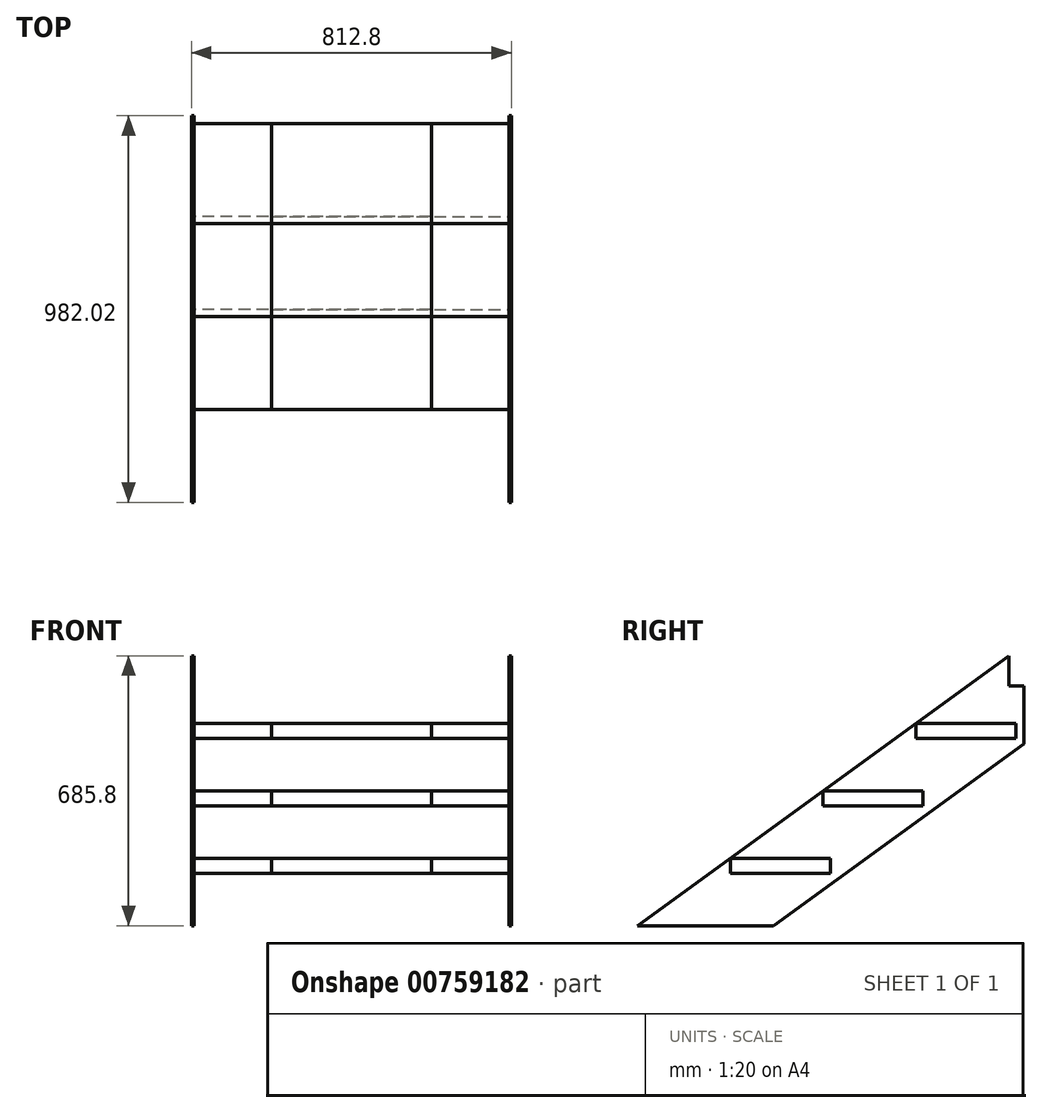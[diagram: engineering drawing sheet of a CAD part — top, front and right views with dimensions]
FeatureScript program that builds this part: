
annotation { "Feature Type Name" : "Feature", "Feature Type Description" : "" }
export const myFeature = defineFeature(function(context is Context, id is Id, definition is map)
    precondition{}
    {
        {
            var Q0;
            Q0=qCreatedBy(makeId("Right.planeOp"),FACE);
            var sketch = newSketch(context, id + "F0", { "sketchPlane" : qUnion([Q0])});
            skLineSegment(sketch, "E0", {"start": v(0, 0) * mm, "end": v(-943.92, 0) * mm});
            skLineSegment(sketch, "E1", {"start": v(0, 685.8) * mm, "end": v(-943.92, 0) * mm});
            skLineSegment(sketch, "E2", {"start": v(-598.22, 0) * mm, "end": v(0, 434.63) * mm});
            skLineSegment(sketch, "E3.bottom", {"start": v(-707.94, 171.45) * mm, "end": v(-453.94, 171.45) * mm});
            skLineSegment(sketch, "E3.top", {"start": v(-707.94, 133.35) * mm, "end": v(-453.94, 133.35) * mm});
            skLineSegment(sketch, "E3.left", {"start": v(-707.94, 171.45) * mm, "end": v(-707.94, 133.35) * mm});
            skLineSegment(sketch, "E3.right", {"start": v(-453.94, 171.45) * mm, "end": v(-453.94, 133.35) * mm});
            skLineSegment(sketch, "E4.bottom", {"start": v(-471.96, 342.9) * mm, "end": v(-217.96, 342.9) * mm});
            skLineSegment(sketch, "E4.top", {"start": v(-471.96, 304.8) * mm, "end": v(-217.96, 304.8) * mm});
            skLineSegment(sketch, "E4.left", {"start": v(-471.96, 342.9) * mm, "end": v(-471.96, 304.8) * mm});
            skLineSegment(sketch, "E4.right", {"start": v(-217.96, 342.9) * mm, "end": v(-217.96, 304.8) * mm});
            skLineSegment(sketch, "E5", {"start": v(0, 685.8) * mm, "end": v(0, 0) * mm});
            skLineSegment(sketch, "E6.bottom", {"start": v(-235.98, 514.35) * mm, "end": v(18.02, 514.35) * mm});
            skLineSegment(sketch, "E6.top", {"start": v(-235.98, 476.25) * mm, "end": v(18.02, 476.25) * mm});
            skLineSegment(sketch, "E6.left", {"start": v(-235.98, 514.35) * mm, "end": v(-235.98, 476.25) * mm});
            skLineSegment(sketch, "E6.right", {"start": v(18.02, 514.35) * mm, "end": v(18.02, 476.25) * mm});
            skLineSegment(sketch, "E7", {"start": v(0, 609.6) * mm, "end": v(38.1, 609.6) * mm});
            skLineSegment(sketch, "E8", {"start": v(38.1, 609.6) * mm, "end": v(38.1, 462.31) * mm});
            skLineSegment(sketch, "E9", {"start": v(38.1, 462.31) * mm, "end": v(0, 434.63) * mm});
            skSolve(sketch);
        }
        {
            var Q0;
            {var subQ15=sQuery(id+"F0.wireOp",EDGE,"E3.top");Q0=makeQuery(id+"F0.imprint","IMPRINT",FACE,{"disambiguationData":[TD([[makeQuery(id+"F0.imprint","IMPRINT",EDGE,{"derivedFrom":subQ15}),-1.0]])]});}
            var Q1;
            {var subQ0=sQuery(id+"F0.wireOp",EDGE,"8nGeiQJS-kXjl-ygCf-tkNA-O2oD8sTWfOC5");var subQ1=sQuery(id+"F0.wireOp",EDGE,"E4.bottom");var subQ2=makeQuery(id+"F0.imprint","INTERSECT",VERTEX,{"derivedFrom":[subQ1,subQ0]});Q1=makeQuery(id+"F0.imprint","IMPRINT",FACE,{"disambiguationData":[TD([[makeQuery(id+"F0.imprint","IMPRINT",EDGE,{"disambiguationData":[TD([[subQ2,1.0]])],"derivedFrom":subQ1}),1.0]])]});}
            var Q2;
            {var subQ1=sQuery(id+"F0.wireOp",EDGE,"E4.top");Q2=makeQuery(id+"F0.imprint","IMPRINT",FACE,{"disambiguationData":[TD([[makeQuery(id+"F0.imprint","IMPRINT",EDGE,{"derivedFrom":subQ1}),1.0]])]});}
            var Q3;
            {var subQ2=sQuery(id+"F0.wireOp",EDGE,"E3.top");Q3=makeQuery(id+"F0.imprint","IMPRINT",FACE,{"disambiguationData":[TD([[makeQuery(id+"F0.imprint","IMPRINT",EDGE,{"derivedFrom":subQ2}),1.0]])]});}
            var Q4;
            {var subQ0=sQuery(id+"F0.wireOp",EDGE,"E3.bottom");var subQ5=sQuery(id+"F0.wireOp",EDGE,"nGp2zIO6-5YUV-txhC-nwUu-UrbXQL7LYUXX");var subQ6=makeQuery(id+"F0.imprint","INTERSECT",VERTEX,{"derivedFrom":[subQ0,subQ5]});Q4=makeQuery(id+"F0.imprint","IMPRINT",FACE,{"disambiguationData":[TD([[makeQuery(id+"F0.imprint","IMPRINT",EDGE,{"disambiguationData":[TD([[subQ6,-1.0]])],"derivedFrom":subQ5}),1.0]])]});}
            var Q5;
            {var subQ1=sQuery(id+"F0.wireOp",EDGE,"E4.bottom");var subQ3=sQuery(id+"F0.wireOp",EDGE,"nGp2zIO6-5YUV-txhC-nwUu-UrbXQL7LYUXX");var subQ4=makeQuery(id+"F0.imprint","INTERSECT",VERTEX,{"derivedFrom":[subQ1,subQ3]});Q5=makeQuery(id+"F0.imprint","IMPRINT",FACE,{"disambiguationData":[TD([[makeQuery(id+"F0.imprint","IMPRINT",EDGE,{"disambiguationData":[TD([[subQ4,1.0]])],"derivedFrom":subQ3}),1.0]])]});}
            var Q6;
            {var subQ5=sQuery(id+"F0.wireOp",EDGE,"nGp2zIO6-5YUV-txhC-nwUu-UrbXQL7LYUXX");var subQ6=sQuery(id+"F0.wireOp",EDGE,"E4.bottom");var subQ7=makeQuery(id+"F0.imprint","INTERSECT",VERTEX,{"derivedFrom":[subQ6,subQ5]});Q6=makeQuery(id+"F0.imprint","IMPRINT",FACE,{"disambiguationData":[TD([[makeQuery(id+"F0.imprint","IMPRINT",EDGE,{"disambiguationData":[TD([[subQ7,-1.0]])],"derivedFrom":subQ6}),-1.0]])]});}
            var Q7;
            {var subQ0=sQuery(id+"F0.wireOp",EDGE,"nGp2zIO6-5YUV-txhC-nwUu-UrbXQL7LYUXX");var subQ1=sQuery(id+"F0.wireOp",EDGE,"E4.bottom");var subQ2=makeQuery(id+"F0.imprint","INTERSECT",VERTEX,{"derivedFrom":[subQ1,subQ0]});Q7=makeQuery(id+"F0.imprint","IMPRINT",FACE,{"disambiguationData":[TD([[makeQuery(id+"F0.imprint","IMPRINT",EDGE,{"disambiguationData":[TD([[subQ2,-1.0]])],"derivedFrom":subQ1}),1.0]])]});}
            var Q8;
            {var subQ5=sQuery(id+"F0.wireOp",EDGE,"E2");Q8=makeQuery(id+"F0.imprint","IMPRINT",FACE,{"disambiguationData":[TD([[makeQuery(id+"F0.imprint","IMPRINT",EDGE,{"derivedFrom":subQ5}),1.0]])]});}
            var Q9;
            {var subQ1=sQuery(id+"F0.wireOp",EDGE,"E3.bottom");var subQ3=sQuery(id+"F0.wireOp",EDGE,"nGp2zIO6-5YUV-txhC-nwUu-UrbXQL7LYUXX");var subQ4=makeQuery(id+"F0.imprint","INTERSECT",VERTEX,{"derivedFrom":[subQ1,subQ3]});Q9=makeQuery(id+"F0.imprint","IMPRINT",FACE,{"disambiguationData":[TD([[makeQuery(id+"F0.imprint","IMPRINT",EDGE,{"disambiguationData":[TD([[subQ4,1.0]])],"derivedFrom":subQ3}),1.0]])]});}
            var Q10;
            {var subQ1=sQuery(id+"F0.wireOp",EDGE,"E0");var subQ5=sQuery(id+"F0.wireOp",EDGE,"E1");var subQ8=makeQuery(id+"F0.imprint","INTERSECT",VERTEX,{"derivedFrom":[subQ1,subQ5]});Q10=makeQuery(id+"F0.imprint","IMPRINT",FACE,{"disambiguationData":[TD([[makeQuery(id+"F0.imprint","IMPRINT",EDGE,{"disambiguationData":[TD([[subQ8,1.0]])],"derivedFrom":subQ1}),-1.0]])]});}
            var Q11;
            {var subQ5=sQuery(id+"F0.wireOp",EDGE,"E6.left");Q11=makeQuery(id+"F0.imprint","IMPRINT",FACE,{"disambiguationData":[TD([[makeQuery(id+"F0.imprint","IMPRINT",EDGE,{"derivedFrom":subQ5}),1.0]])]});}
            var Q12;
            {var subQ0=sQuery(id+"F0.wireOp",EDGE,"E5");var subQ1=sQuery(id+"F0.wireOp",EDGE,"E1");var subQ2=makeQuery(id+"F0.imprint","INTERSECT",VERTEX,{"derivedFrom":[subQ1,subQ0]});Q12=makeQuery(id+"F0.imprint","IMPRINT",FACE,{"disambiguationData":[TD([[makeQuery(id+"F0.imprint","IMPRINT",EDGE,{"disambiguationData":[TD([[subQ2,-1.0]])],"derivedFrom":subQ0}),-1.0]])]});}
            var Q13;
            {var subQ0=sQuery(id+"F0.wireOp",EDGE,"E6.right");Q13=makeQuery(id+"F0.imprint","IMPRINT",FACE,{"disambiguationData":[TD([[makeQuery(id+"F0.imprint","IMPRINT",EDGE,{"derivedFrom":subQ0}),1.0]])]});}
            var Q14;
            {var subQ5=sQuery(id+"F0.wireOp",EDGE,"E6.right");Q14=makeQuery(id+"F0.imprint","IMPRINT",FACE,{"disambiguationData":[TD([[makeQuery(id+"F0.imprint","IMPRINT",EDGE,{"derivedFrom":subQ5}),-1.0]])]});}
            extrude(context, id + "F1", {"entities" : qUnion([Q0, Q1, Q2, Q3, Q4, Q5, Q6, Q7, Q8, Q9, Q10, Q11, Q12, Q13, Q14]), "oppositeDirection" : true, "depth" : 6.35 * mm, "offsetDistance" : 25.4 * mm});
        }
        {
            var Q0;
            Q0=qCreatedBy(makeId("Right.planeOp"),FACE);
            cPlane(context, id + "F2", {"entities" : qUnion([Q0]), "cplaneType" : CPlaneType.OFFSET, "offset" : 406.4 * mm, "oppositeDirection" : true, "width" : 152.4 * mm, "height" : 152.4 * mm});
        }
        {
            var Q0;
            {var subQ1=sQuery(id+"F0.wireOp",EDGE,"E4.top");Q0=makeQuery(id+"F0.imprint","IMPRINT",FACE,{"disambiguationData":[TD([[makeQuery(id+"F0.imprint","IMPRINT",EDGE,{"derivedFrom":subQ1}),1.0]])]});}
            var Q1;
            {var subQ2=sQuery(id+"F0.wireOp",EDGE,"E3.top");Q1=makeQuery(id+"F0.imprint","IMPRINT",FACE,{"disambiguationData":[TD([[makeQuery(id+"F0.imprint","IMPRINT",EDGE,{"derivedFrom":subQ2}),1.0]])]});}
            var Q2;
            {var subQ5=sQuery(id+"F0.wireOp",EDGE,"nGp2zIO6-5YUV-txhC-nwUu-UrbXQL7LYUXX");var subQ6=sQuery(id+"F0.wireOp",EDGE,"E4.bottom");var subQ7=makeQuery(id+"F0.imprint","INTERSECT",VERTEX,{"derivedFrom":[subQ6,subQ5]});Q2=makeQuery(id+"F0.imprint","IMPRINT",FACE,{"disambiguationData":[TD([[makeQuery(id+"F0.imprint","IMPRINT",EDGE,{"disambiguationData":[TD([[subQ7,-1.0]])],"derivedFrom":subQ6}),-1.0]])]});}
            var Q3;
            {var subQ5=sQuery(id+"F0.wireOp",EDGE,"E6.left");Q3=makeQuery(id+"F0.imprint","IMPRINT",FACE,{"disambiguationData":[TD([[makeQuery(id+"F0.imprint","IMPRINT",EDGE,{"derivedFrom":subQ5}),1.0]])]});}
            var Q4;
            {var subQ5=sQuery(id+"F0.wireOp",EDGE,"E6.right");Q4=makeQuery(id+"F0.imprint","IMPRINT",FACE,{"disambiguationData":[TD([[makeQuery(id+"F0.imprint","IMPRINT",EDGE,{"derivedFrom":subQ5}),-1.0]])]});}
            extrude(context, id + "F3", {"entities" : qUnion([Q0, Q1, Q2, Q3, Q4]), "oppositeDirection" : true, "depth" : 609.6 * mm, "offsetDistance" : 25.4 * mm});
        }
        {
            var Q0;
            Q0=qCreatedBy(makeId("Front.planeOp"),FACE);
            var sketch = newSketch(context, id + "F4", { "sketchPlane" : qUnion([Q0])});
            skCircle(sketch, "E10", {"center": v(-19.05, 644.53) * mm, "radius": 11.11 * mm});
            skSolve(sketch);
        }
        {
            var Q0;
            Q0 = qSketchRegion(id + "F4", true);
            extrude(context, id + "F5", {"entities" : qUnion([Q0]), "operationType" : NewBodyOperationType.REMOVE, "depth" : 12.7 * mm, "offsetDistance" : 25.4 * mm});
        }
        {
            var Q0;
            Q0=makeQuery(id+"F1.opExtrude","SWEPT_BODY",BODY,{"disambiguationData":[OSD([sQuery(id+"F0.wireOp",EDGE,"E0"),sQuery(id+"F0.wireOp",EDGE,"E1"),sQuery(id+"F0.wireOp",EDGE,"E2"),sQuery(id+"F0.wireOp",EDGE,"E5")])]});
            var Q1;
            Q1=makeQuery(id+"F3.opExtrude","SWEPT_BODY",BODY,{"disambiguationData":[OSD([sQuery(id+"F0.wireOp",EDGE,"E4.bottom"),sQuery(id+"F0.wireOp",EDGE,"E4.top"),sQuery(id+"F0.wireOp",EDGE,"E4.left"),sQuery(id+"F0.wireOp",EDGE,"E4.right")])]});
            var Q2;
            Q2=makeQuery(id+"F3.opExtrude","SWEPT_BODY",BODY,{"disambiguationData":[OSD([sQuery(id+"F0.wireOp",EDGE,"E3.bottom"),sQuery(id+"F0.wireOp",EDGE,"E3.top"),sQuery(id+"F0.wireOp",EDGE,"E3.left"),sQuery(id+"F0.wireOp",EDGE,"E3.right")])]});
            var Q3;
            Q3=makeQuery(id+"F3.opExtrude","SWEPT_BODY",BODY,{"disambiguationData":[OSD([sQuery(id+"F0.wireOp",EDGE,"E6.bottom"),sQuery(id+"F0.wireOp",EDGE,"E6.top"),sQuery(id+"F0.wireOp",EDGE,"E6.left"),sQuery(id+"F0.wireOp",EDGE,"E6.right")])]});
            var Q4;
            Q4=qCreatedBy(id+"F2.planeOp",FACE);
            mirror(context, id + "F6", {"entities" : qUnion([Q0, Q1, Q2, Q3]), "mirrorPlane" : qUnion([Q4])});
        }
    });
